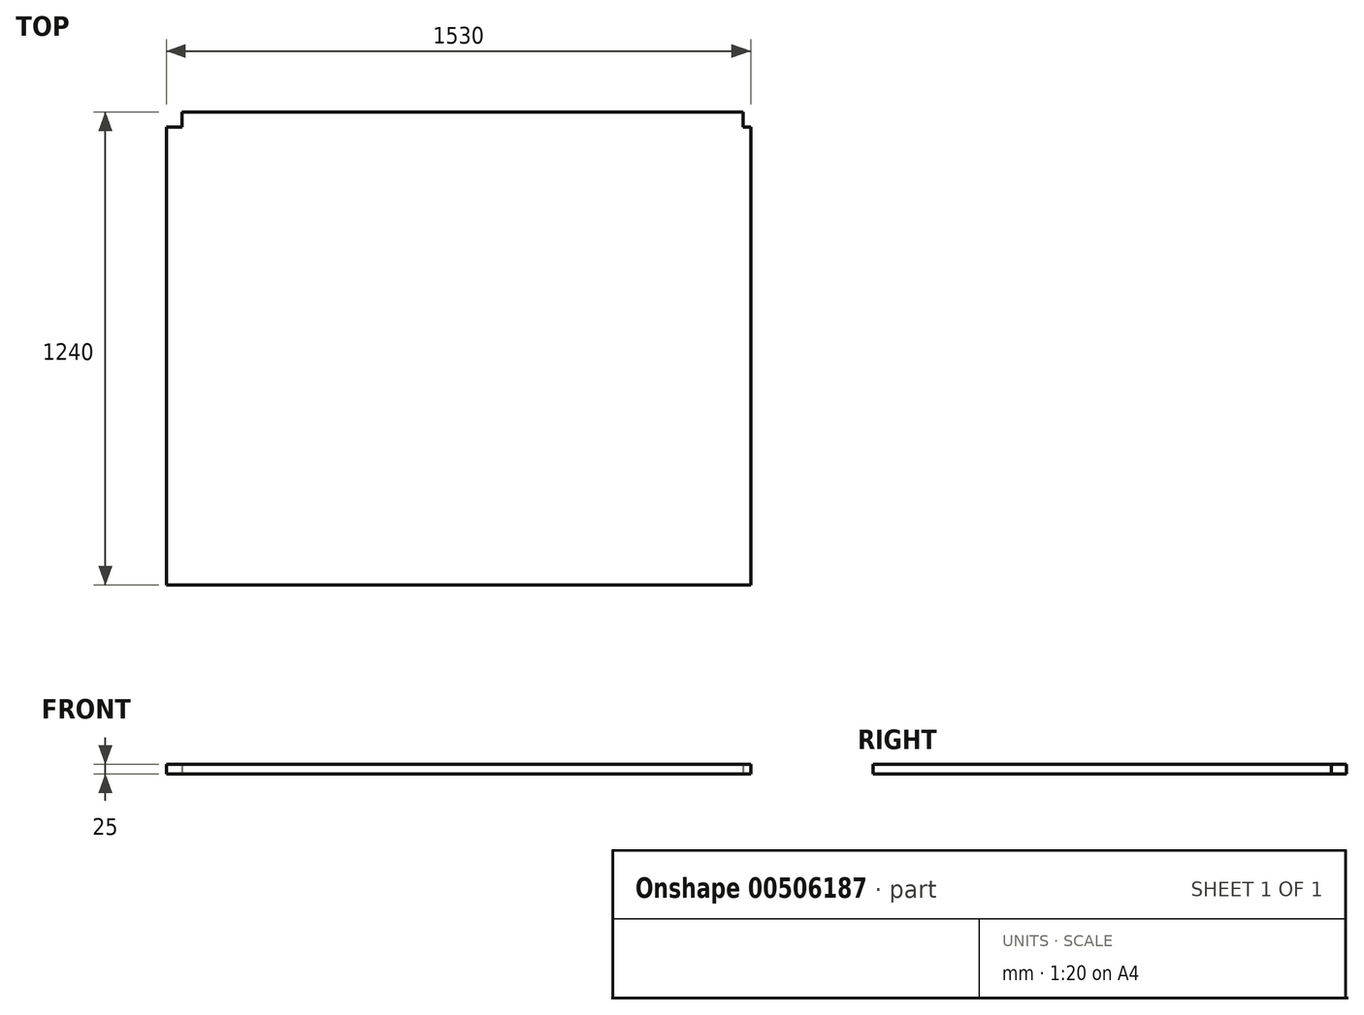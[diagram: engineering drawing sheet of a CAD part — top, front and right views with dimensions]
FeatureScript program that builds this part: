
annotation { "Feature Type Name" : "Feature", "Feature Type Description" : "" }
export const myFeature = defineFeature(function(context is Context, id is Id, definition is map)
    precondition{}
    {
        {
            var Q0;
            Q0=qCreatedBy(makeId("Top.planeOp"),FACE);
            var sketch = newSketch(context, id + "F0", { "sketchPlane" : qUnion([Q0])});
            skLineSegment(sketch, "E0.bottom", {"start": v(765, 620) * mm, "end": v(-765, 620) * mm});
            skLineSegment(sketch, "E0.top", {"start": v(765, -620) * mm, "end": v(-765, -620) * mm});
            skLineSegment(sketch, "E0.left", {"start": v(765, 620) * mm, "end": v(765, -620) * mm});
            skLineSegment(sketch, "E0.right", {"start": v(-765, 620) * mm, "end": v(-765, -620) * mm});
            skPoint(sketch, "E0.middle", {"position": v(0, 0) * mm});
            skLineSegment(sketch, "E1", {"start": v(-725, 620) * mm, "end": v(-725, 580) * mm});
            skLineSegment(sketch, "E2", {"start": v(-725, 580) * mm, "end": v(-765, 580) * mm});
            skLineSegment(sketch, "E3", {"start": v(745, 620) * mm, "end": v(745, 580) * mm});
            skPoint(sketch, "E3.endSnap0", {"position": v(-745, 580) * mm});
            skLineSegment(sketch, "E4", {"start": v(745, 580) * mm, "end": v(765, 580) * mm});
            skLineSegment(sketch, "E5.MirrorCS", {"start": v(-725, -580) * mm, "end": v(-765, -580) * mm});
            skLineSegment(sketch, "E6.MirrorCS", {"start": v(-725, -620) * mm, "end": v(-725, -580) * mm});
            skLineSegment(sketch, "E7.MirrorCS", {"start": v(745, -620) * mm, "end": v(745, -580) * mm});
            skLineSegment(sketch, "E8.MirrorCS", {"start": v(745, -580) * mm, "end": v(765, -580) * mm});
            skSolve(sketch);
        }
        {
            var Q0;
            {var subQ4=sQuery(id+"F0.wireOp",EDGE,"E1");Q0=makeQuery(id+"F0.imprint","IMPRINT",FACE,{"disambiguationData":[TD([[makeQuery(id+"F0.imprint","IMPRINT",EDGE,{"derivedFrom":subQ4}),1.0]])]});}
            var Q1;
            {var subQ4=sQuery(id+"F0.wireOp",EDGE,"E5.MirrorCS");Q1=makeQuery(id+"F0.imprint","IMPRINT",FACE,{"disambiguationData":[TD([[makeQuery(id+"F0.imprint","IMPRINT",EDGE,{"derivedFrom":subQ4}),1.0]])]});}
            var Q2;
            {var subQ3=sQuery(id+"F0.wireOp",EDGE,"E7.MirrorCS");Q2=makeQuery(id+"F0.imprint","IMPRINT",FACE,{"disambiguationData":[TD([[makeQuery(id+"F0.imprint","IMPRINT",EDGE,{"derivedFrom":subQ3}),-1.0]])]});}
            extrude(context, id + "F1", {"entities" : qUnion([Q0, Q1, Q2]), "depth" : 25 * mm});
        }
    });
